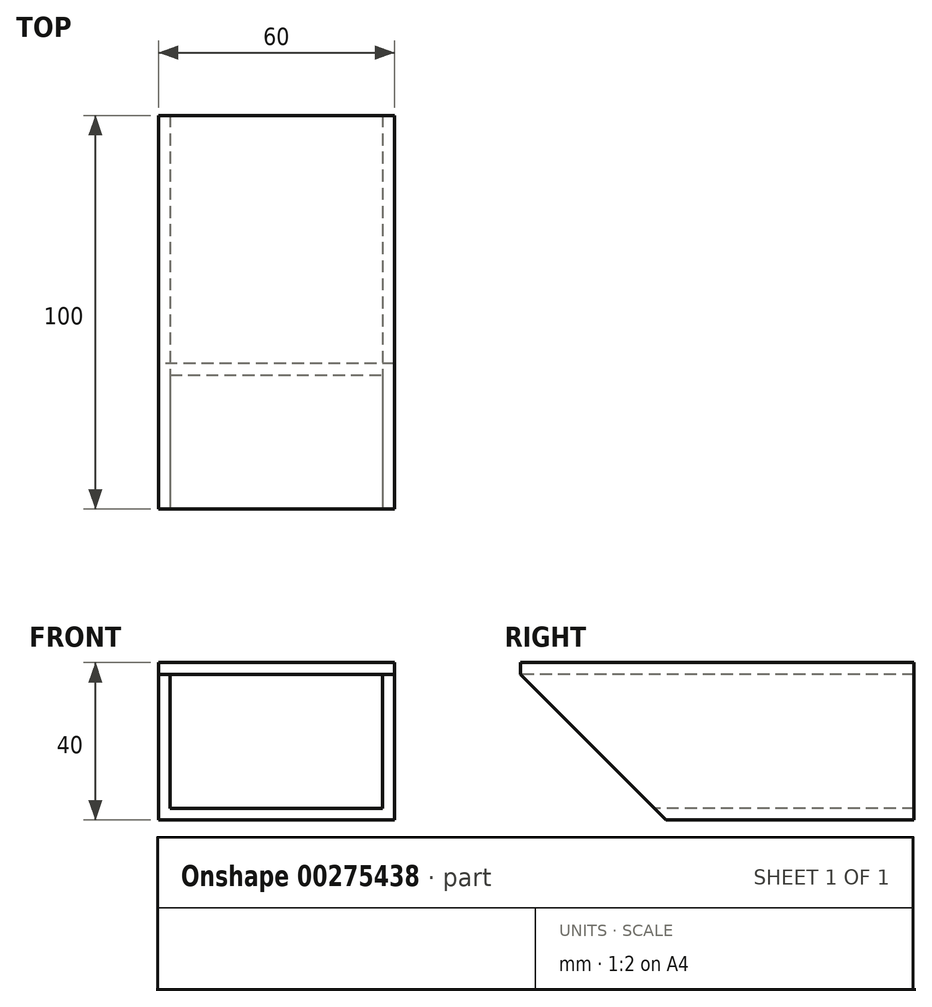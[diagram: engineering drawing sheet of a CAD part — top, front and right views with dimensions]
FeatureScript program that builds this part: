
annotation { "Feature Type Name" : "Feature", "Feature Type Description" : "" }
export const myFeature = defineFeature(function(context is Context, id is Id, definition is map)
    precondition{}
    {
        {
            var Q0;
            Q0=qCreatedBy(makeId("Top.planeOp"),FACE);
            var sketch = newSketch(context, id + "F0", { "sketchPlane" : qUnion([Q0])});
            skLineSegment(sketch, "E0.bottom", {"start": v(30, 50) * mm, "end": v(-30, 50) * mm});
            skLineSegment(sketch, "E0.top", {"start": v(30, -50) * mm, "end": v(-30, -50) * mm});
            skLineSegment(sketch, "E0.left", {"start": v(30, 50) * mm, "end": v(30, -50) * mm});
            skLineSegment(sketch, "E0.right", {"start": v(-30, 50) * mm, "end": v(-30, -50) * mm});
            skPoint(sketch, "E0.middle", {"position": v(0, 0) * mm});
            skSolve(sketch);
        }
        {
            var Q0;
            Q0=qSketchRegion(id+"F0",true);
            var Q1;
            Q1=makeQuery(id+"F0.imprint","IMPRINT",FACE,{"disambiguationData":[TD([[makeQuery(id+"F0.imprint","IMPRINT",EDGE,{"derivedFrom":sQuery(id+"F0.wireOp",EDGE,"E0.bottom")}),1.0]])]});
            extrude(context, id + "F1", {"entities" : qUnion([Q0, Q1]), "depth" : 40 * mm});
        }
        {
            var Q0;
            Q0=makeQuery(id+"F1.opExtrude","SWEPT_FACE",FACE,{"disambiguationData":[OSD([sQuery(id+"F0.wireOp",EDGE,"E0.top")])]});
            var sketch = newSketch(context, id + "F2", { "sketchPlane" : qUnion([Q0])});
            skLineSegment(sketch, "E1.bottom", {"start": v(27, 37) * mm, "end": v(-27, 37) * mm});
            skLineSegment(sketch, "E1.top", {"start": v(27, 3) * mm, "end": v(-27, 3) * mm});
            skLineSegment(sketch, "E1.left", {"start": v(27, 37) * mm, "end": v(27, 3) * mm});
            skLineSegment(sketch, "E1.right", {"start": v(-27, 37) * mm, "end": v(-27, 3) * mm});
            skPoint(sketch, "E1.middle", {"position": v(0, 20) * mm});
            skPoint(sketch, "E1.middle.positionSnap0", {"position": v(30, 20) * mm});
            skPoint(sketch, "E1.centerSnap0", {"position": v(30, 20) * mm});
            skSolve(sketch);
        }
        {
            var Q0;
            Q0=makeQuery(id+"F2.imprint","IMPRINT",FACE,{"disambiguationData":[TD([[makeQuery(id+"F2.imprint","IMPRINT",EDGE,{"derivedFrom":sQuery(id+"F2.wireOp",EDGE,"E1.bottom")}),1.0]])]});
            extrude(context, id + "F3", {"entities" : qUnion([Q0]), "operationType" : NewBodyOperationType.REMOVE, "oppositeDirection" : true, "depth" : 141 * mm});
        }
        {
            var Q0;
            Q0=makeQuery(id+"F1.opExtrude","SWEPT_FACE",FACE,{"disambiguationData":[OSD([sQuery(id+"F0.wireOp",EDGE,"E0.right")])]});
            var sketch = newSketch(context, id + "F4", { "sketchPlane" : qUnion([Q0])});
            skPoint(sketch, "E2", {"position": v(13, 0) * mm});
            skPoint(sketch, "E3", {"position": v(50, 37) * mm});
            skLineSegment(sketch, "E4", {"start": v(13, 0) * mm, "end": v(50, 37) * mm});
            skLineSegment(sketch, "E5", {"start": v(50, 0) * mm, "end": v(13, 0) * mm});
            skLineSegment(sketch, "E6", {"start": v(50, 0) * mm, "end": v(50, 37) * mm});
            skSolve(sketch);
        }
        {
            var Q0;
            Q0=makeQuery(id+"F4.imprint","IMPRINT",FACE,{"disambiguationData":[TD([[makeQuery(id+"F4.imprint","IMPRINT",EDGE,{"derivedFrom":sQuery(id+"F4.wireOp",EDGE,"E4")}),-1.0]])]});
            extrude(context, id + "F5", {"entities" : qUnion([Q0]), "operationType" : NewBodyOperationType.REMOVE, "oppositeDirection" : true, "depth" : 60 * mm});
        }
    });
